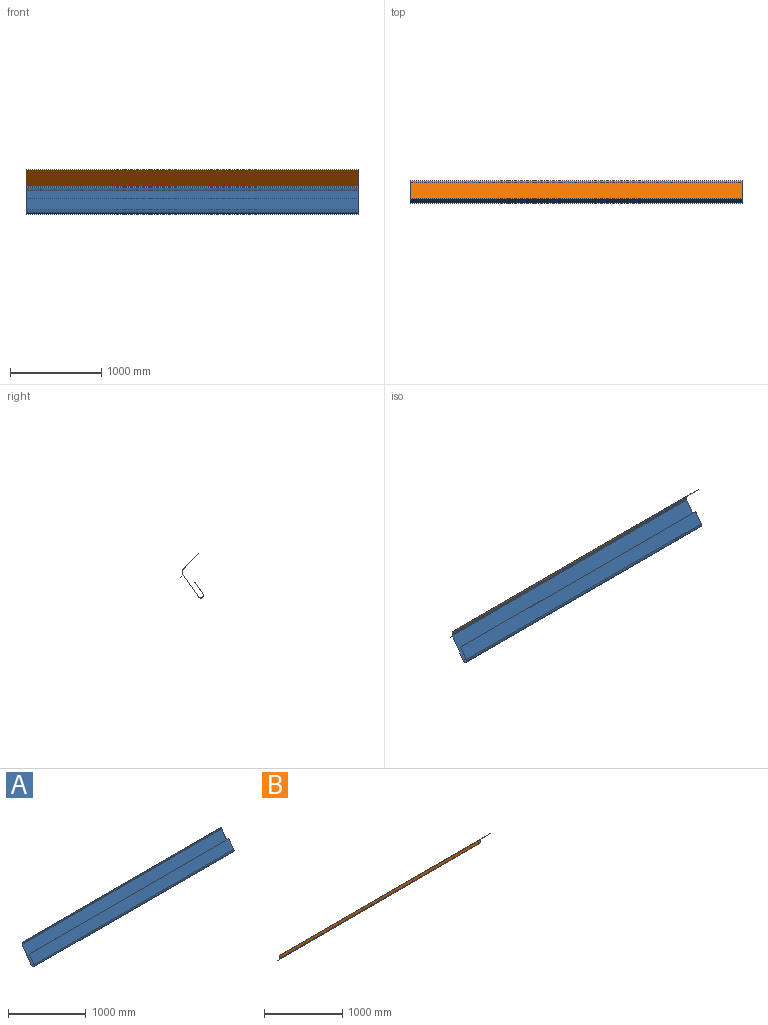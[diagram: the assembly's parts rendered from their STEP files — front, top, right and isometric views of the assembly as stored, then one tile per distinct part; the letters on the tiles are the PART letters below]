
ASSEMBLY  parts=2 mates=1
PART A: 37 faces, bbox 3640x226.3x288.5 mm
  f0: cylinder r=1.5mm len=3mm, axis (0,-1,0), area 7.5mm2, adj f31,f33
  f1: cylinder r=1.5mm len=3mm, axis (0,-1,0), area 7.5mm2, adj f31,f33
  f2: cylinder r=1.5mm len=3mm, axis (0,-1,0), area 7.5mm2, adj f31,f33
  f3: cylinder r=1.5mm len=3mm, axis (0,-1,0), area 7.5mm2, adj f31,f33
  f4: cylinder r=1.5mm len=3mm, axis (0,-1,0), area 7.5mm2, adj f31,f33
  f5: cylinder r=1.5mm len=3mm, axis (0,-1,0), area 7.5mm2, adj f31,f33
  f6: cylinder r=1.5mm len=3mm, axis (0,-1,0), area 7.5mm2, adj f31,f33
  f7: cylinder r=1.5mm len=3mm, axis (0,-1,0), area 7.5mm2, adj f31,f33
  f8: cylinder r=1.5mm len=3mm, axis (0,-1,0), area 7.5mm2, adj f31,f33
  f9: cylinder r=1.5mm len=3mm, axis (0,-1,0), area 7.5mm2, adj f31,f33
  f10: cylinder r=1.5mm len=3mm, axis (0,-1,0), area 7.5mm2, adj f31,f33
  f11: cylinder r=1.5mm len=3mm, axis (0,-1,0), area 7.5mm2, adj f31,f33
  f12: cylinder r=1.5mm len=3mm, axis (0,-1,0), area 7.5mm2, adj f31,f33
  f13: cylinder r=1.5mm len=3mm, axis (0,-1,0), area 7.5mm2, adj f31,f33
  f14: cylinder r=1.5mm len=3mm, axis (0,-1,0), area 7.5mm2, adj f31,f33
  f15: cylinder r=1.5mm len=3mm, axis (0,-1,0), area 7.5mm2, adj f31,f33
  f16: cylinder r=1.5mm len=3mm, axis (0,-1,0), area 7.5mm2, adj f31,f33
  f17: cylinder r=1.5mm len=3mm, axis (0,-1,0), area 7.5mm2, adj f31,f33
  f18: cylinder r=1.5mm len=3mm, axis (0,-1,0), area 7.5mm2, adj f31,f33
  f19: cylinder r=1.5mm len=3mm, axis (0,-1,0), area 7.5mm2, adj f31,f33
  f20: cylinder r=1.5mm len=3mm, axis (0,-1,0), area 7.5mm2, adj f31,f33
  f21: cylinder r=1.5mm len=3mm, axis (0,-1,0), area 7.5mm2, adj f31,f33
  f22: cylinder r=1.5mm len=3mm, axis (0,-1,0), area 7.5mm2, adj f31,f33
  f23: cylinder r=1.5mm len=3mm, axis (0,-1,0), area 7.5mm2, adj f31,f33
  f24: plane 3640x245.54mm, normal (0,-0.82,0.57), area 1091081.9mm2, adj f25,f33,f34,f35
  f25: cylinder r=29mm len=3640mm, axis (-1,0,0), area 331626.5mm2, adj f24,f26,f34,f35
  f26: plane 3640x122.87mm, normal (0,0.82,-0.57), area 546000mm2, adj f25,f27,f34,f35
  f27: plane 3640x0.66mm, normal (0,0.57,0.82), area 2912mm2, adj f26,f28,f34,f35
  f28: plane 3640x122.87mm, normal (0,-0.82,0.57), area 546000mm2, adj f27,f29,f34,f35
  f29: cylinder r=29.8mm len=3640mm, axis (-1,0,0), area 340774.8mm2, adj f28,f30,f34,f35
  f30: plane 3640x245.75mm, normal (0,0.82,-0.57), area 1092000mm2, adj f29,f31,f34,f35
  f31: plane 3640x30mm, normal (0,1,0), area 109023.3mm2, adj f0,f1,f2,f3,f4,f5,f6,f7
  f32: plane 3640x0.8mm, normal (0,0,1), area 2912mm2, adj f31,f33,f34,f35
  f33: plane 3640x29.75mm, normal (0,-1,0), area 108105.1mm2, adj f0,f1,f2,f3,f4,f5,f6,f7
  f34: plane 288.45x226.28mm, normal (1,0,0), area 457.7mm2, adj f24,f25,f26,f27,f28,f29,f30,f31
  f35: plane 288.45x226.28mm, normal (-1,0,0), area 457.7mm2, adj f24,f25,f26,f27,f28,f29,f30,f31
  f36: cylinder r=1.5mm len=3mm, axis (0,-1,0), area 7.5mm2, adj f31,f33
PART B: 35 faces, bbox 3640x200.1x259.5 mm
  f0: cylinder r=1.5mm len=3mm, axis (0,-1,0), area 7.5mm2, adj f25,f29
  f1: cylinder r=1.5mm len=3mm, axis (0,-1,0), area 7.5mm2, adj f25,f29
  f2: cylinder r=1.5mm len=3mm, axis (0,-1,0), area 7.5mm2, adj f25,f29
  f3: cylinder r=1.5mm len=3mm, axis (0,-1,0), area 7.5mm2, adj f25,f29
  f4: cylinder r=1.5mm len=3mm, axis (0,-1,0), area 7.5mm2, adj f25,f29
  f5: cylinder r=1.5mm len=3mm, axis (0,-1,0), area 7.5mm2, adj f25,f29
  f6: cylinder r=1.5mm len=3mm, axis (0,-1,0), area 7.5mm2, adj f25,f29
  f7: cylinder r=1.5mm len=3mm, axis (0,-1,0), area 7.5mm2, adj f25,f29
  f8: cylinder r=1.5mm len=3mm, axis (0,-1,0), area 7.5mm2, adj f25,f29
  f9: cylinder r=1.5mm len=3mm, axis (0,-1,0), area 7.5mm2, adj f25,f29
  f10: cylinder r=1.5mm len=3mm, axis (0,-1,0), area 7.5mm2, adj f25,f29
  f11: cylinder r=1.5mm len=3mm, axis (0,-1,0), area 7.5mm2, adj f25,f29
  f12: cylinder r=1.5mm len=3mm, axis (0,-1,0), area 7.5mm2, adj f25,f29
  f13: cylinder r=1.5mm len=3mm, axis (0,-1,0), area 7.5mm2, adj f25,f29
  f14: cylinder r=1.5mm len=3mm, axis (0,-1,0), area 7.5mm2, adj f25,f29
  f15: cylinder r=1.5mm len=3mm, axis (0,-1,0), area 7.5mm2, adj f25,f29
  f16: cylinder r=1.5mm len=3mm, axis (0,-1,0), area 7.5mm2, adj f25,f29
  f17: cylinder r=1.5mm len=3mm, axis (0,-1,0), area 7.5mm2, adj f25,f29
  f18: cylinder r=1.5mm len=3mm, axis (0,-1,0), area 7.5mm2, adj f25,f29
  f19: cylinder r=1.5mm len=3mm, axis (0,-1,0), area 7.5mm2, adj f25,f29
  f20: cylinder r=1.5mm len=3mm, axis (0,-1,0), area 7.5mm2, adj f25,f29
  f21: cylinder r=1.5mm len=3mm, axis (0,-1,0), area 7.5mm2, adj f25,f29
  f22: cylinder r=1.5mm len=3mm, axis (0,-1,0), area 7.5mm2, adj f25,f29
  f23: cylinder r=1.5mm len=3mm, axis (0,-1,0), area 7.5mm2, adj f25,f29
  f24: plane 3640x176.54mm, normal (0,-0.71,-0.71), area 908793.8mm2, adj f25,f31,f32,f33
  f25: plane 3640x49.67mm, normal (0,-1,0), area 180617.1mm2, adj f0,f1,f2,f3,f4,f5,f6,f7
  f26: plane 3640x32.77mm, normal (0,-0.82,-0.57), area 145600mm2, adj f25,f27,f32,f33
  f27: plane 3640x0.66mm, normal (0,0.57,-0.82), area 2912mm2, adj f26,f28,f32,f33
  f28: plane 3640x32.56mm, normal (0,0.82,0.57), area 144681.9mm2, adj f27,f29,f32,f33
  f29: plane 3640x49.75mm, normal (0,1,0), area 180905.1mm2, adj f0,f1,f2,f3,f4,f5,f6,f7
  f30: plane 3640x176.78mm, normal (0,0.71,0.71), area 910000mm2, adj f29,f31,f32,f33
  f31: plane 3640x0.57mm, normal (0,-0.71,0.71), area 2912mm2, adj f24,f30,f32,f33
  f32: plane 259.54x200.14mm, normal (1,0,0), area 271.5mm2, adj f24,f25,f26,f27,f28,f29,f30,f31
  f33: plane 259.54x200.14mm, normal (-1,0,0), area 271.5mm2, adj f24,f25,f26,f27,f28,f29,f30,f31
  f34: cylinder r=1.5mm len=3mm, axis (0,-1,0), area 7.5mm2, adj f25,f29
PLACE A at identity fixed
PLACE B at identity
MATE fastened B.f25 <-> A.f31  axis (0,-1,0) through (3640,0,0)mm
